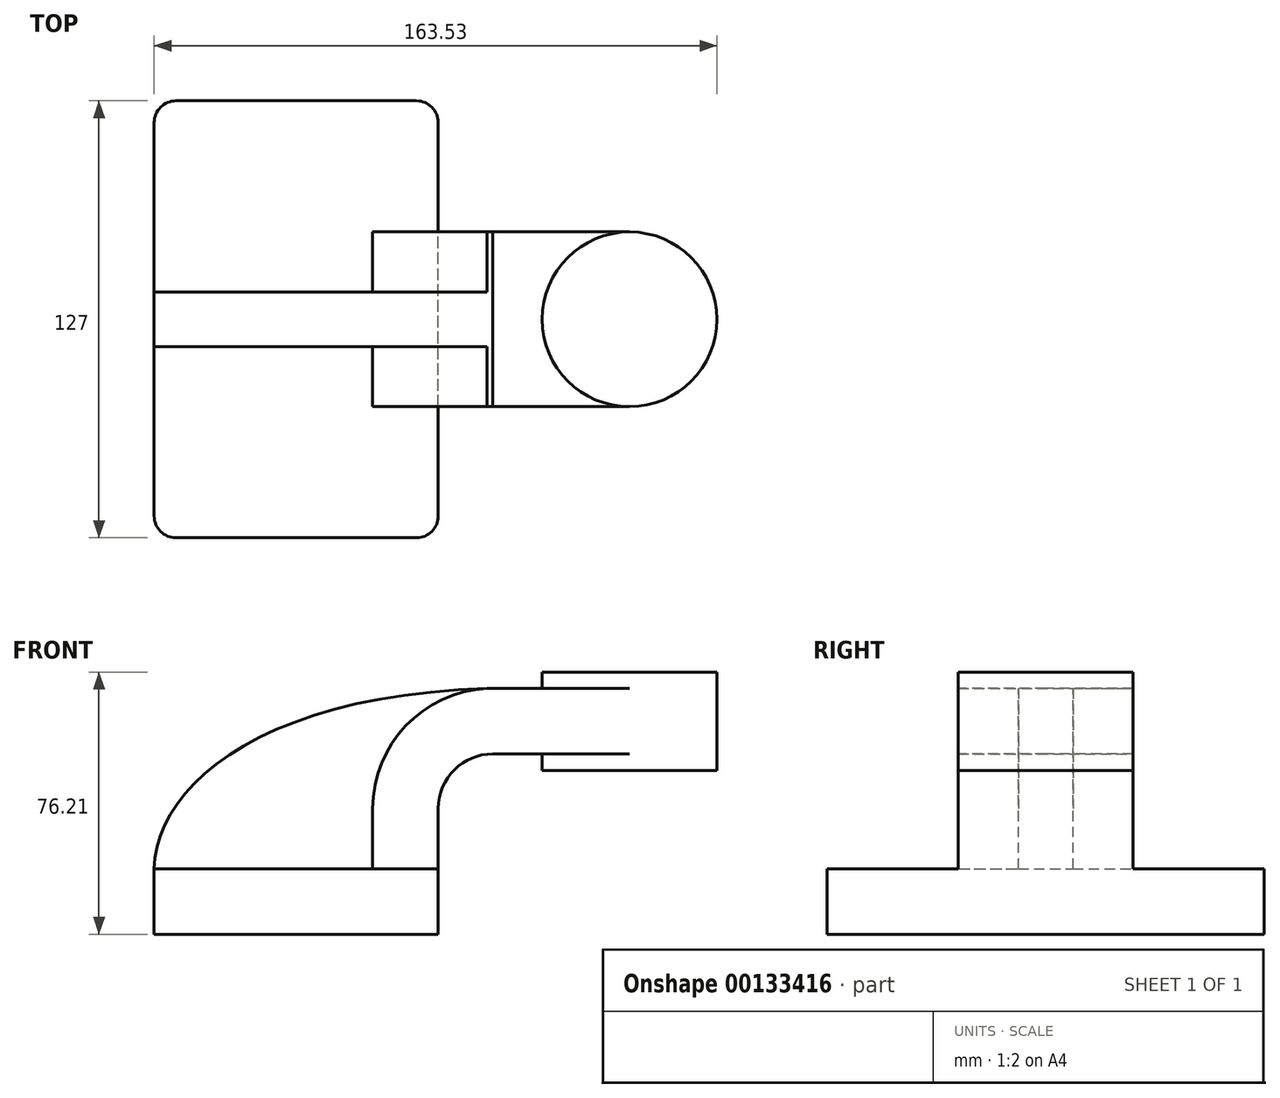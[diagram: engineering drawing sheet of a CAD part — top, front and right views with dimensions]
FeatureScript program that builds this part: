
annotation { "Feature Type Name" : "Feature", "Feature Type Description" : "" }
export const myFeature = defineFeature(function(context is Context, id is Id, definition is map)
    precondition{}
    {
        {
            var Q0;
            Q0=qCreatedBy(makeId("Front.planeOp"),FACE);
            var sketch = newSketch(context, id + "F0", { "sketchPlane" : qUnion([Q0])});
            skLineSegment(sketch, "E0.bottom", {"start": v(41.28, -9.52) * mm, "end": v(-41.27, -9.53) * mm});
            skLineSegment(sketch, "E0.top", {"start": v(41.27, 9.53) * mm, "end": v(-41.28, 9.53) * mm});
            skLineSegment(sketch, "E0.left", {"start": v(41.28, -9.52) * mm, "end": v(41.28, 9.53) * mm});
            skLineSegment(sketch, "E0.right", {"start": v(-41.27, -9.53) * mm, "end": v(-41.28, 9.53) * mm});
            skPoint(sketch, "E0.middle", {"position": v(0, 0) * mm});
            skLineSegment(sketch, "E1.bottom", {"start": v(122.25, 38.1) * mm, "end": v(71.45, 38.1) * mm});
            skLineSegment(sketch, "E1.top", {"start": v(122.25, 66.68) * mm, "end": v(71.45, 66.68) * mm});
            skLineSegment(sketch, "E1.left", {"start": v(122.25, 38.1) * mm, "end": v(122.25, 66.68) * mm});
            skLineSegment(sketch, "E1.right", {"start": v(71.45, 38.1) * mm, "end": v(71.45, 66.68) * mm});
            skPoint(sketch, "E1.middle", {"position": v(96.85, 52.39) * mm});
            skLineSegment(sketch, "E2", {"start": v(41.27, 9.53) * mm, "end": v(41.27, 27) * mm});
            skArc(sketch, "E3", {"start": v(41.27, 27) * mm, "mid": v(45.92, 38.23) * mm, "end": v(57.15, 42.88) * mm});
            skLineSegment(sketch, "E4", {"start": v(57.15, 42.88) * mm, "end": v(96.85, 42.88) * mm});
            skLineSegment(sketch, "E5.0", {"start": v(57.15, 61.93) * mm, "end": v(96.85, 61.93) * mm});
            skArc(sketch, "E5.1", {"start": v(22.23, 27) * mm, "mid": v(32.45, 51.7) * mm, "end": v(57.15, 61.93) * mm});
            skLineSegment(sketch, "E5.2", {"start": v(22.22, 9.53) * mm, "end": v(22.22, 27) * mm});
            skFitSpline(sketch, "E6", {"points": [v(-41.28, 9.52) * mm, v(57.15, 61.93) * mm], "startDerivative": vector(1.84, 72.05) * mm, "endDerivative": vector(201.06, 4.4) * mm});
            skLineSegment(sketch, "E7", {"start": v(96.85, 38.1) * mm, "end": v(96.85, 66.68) * mm});
            skSolve(sketch);
        }
        {
            var Q0;
            Q0=makeQuery(id+"F0.imprint","IMPRINT",FACE,{"disambiguationData":[TD([[makeQuery(id+"F0.imprint","IMPRINT",EDGE,{"derivedFrom":sQuery(id+"F0.wireOp",EDGE,"E0.bottom")}),-1.0]])]});
            extrude(context, id + "F1", {"entities" : qUnion([Q0]), "endBound" : BoundingType.SYMMETRIC, "depth" : 127 * mm});
        }
        {
            var Q0;
            {var subQ1=sQuery(id+"F0.wireOp",EDGE,"E2");Q0=makeQuery(id+"F0.imprint","IMPRINT",FACE,{"disambiguationData":[TD([[makeQuery(id+"F0.imprint","IMPRINT",EDGE,{"derivedFrom":subQ1}),1.0]])]});}
            var Q1;
            {var subQ0=sQuery(id+"F0.wireOp",EDGE,"E4");var subQ1=sQuery(id+"F0.wireOp",EDGE,"E1.right");var subQ2=makeQuery(id+"F0.imprint","INTERSECT",VERTEX,{"derivedFrom":[subQ1,subQ0]});Q1=makeQuery(id+"F0.imprint","IMPRINT",FACE,{"disambiguationData":[TD([[makeQuery(id+"F0.imprint","IMPRINT",EDGE,{"disambiguationData":[TD([[subQ2,-1.0]])],"derivedFrom":subQ1}),-1.0]])]});}
            extrude(context, id + "F2", {"entities" : qUnion([Q0, Q1]), "operationType" : NewBodyOperationType.ADD, "endBound" : BoundingType.SYMMETRIC, "depth" : 50.8 * mm});
        }
        {
            var Q0;
            {var subQ3=sQuery(id+"F0.wireOp",EDGE,"E5.2");Q0=makeQuery(id+"F0.imprint","IMPRINT",FACE,{"disambiguationData":[TD([[makeQuery(id+"F0.imprint","IMPRINT",EDGE,{"derivedFrom":subQ3}),1.0]])]});}
            extrude(context, id + "F3", {"entities" : qUnion([Q0]), "operationType" : NewBodyOperationType.ADD, "endBound" : BoundingType.SYMMETRIC, "depth" : 15.88 * mm});
        }
        {
            var Q0;
            {var subQ4=sQuery(id+"F0.wireOp",EDGE,"E1.left");Q0=makeQuery(id+"F0.imprint","IMPRINT",FACE,{"disambiguationData":[TD([[makeQuery(id+"F0.imprint","IMPRINT",EDGE,{"derivedFrom":subQ4}),1.0]])]});}
            var Q1;
            Q1=sQuery(id+"F0.wireOp",EDGE,"E7");
            revolve(context, id + "F4", {"operationType" : NewBodyOperationType.ADD, "entities" : qUnion([Q0]), "axis" : qUnion([Q1]), "revolveType" : RevolveType.FULL});
        }
        {
            var Q0;
            Q0=makeQuery(id+"F1.opExtrude","CAP_EDGE",EDGE,{"disambiguationData":[OSD([sQuery(id+"F0.wireOp",EDGE,"E0.right")])],"isStart":false});
            var Q1;
            Q1=makeQuery(id+"F1.opExtrude","CAP_EDGE",EDGE,{"disambiguationData":[OSD([sQuery(id+"F0.wireOp",EDGE,"E0.left")])],"isStart":false});
            var Q2;
            Q2=makeQuery(id+"F1.opExtrude","CAP_EDGE",EDGE,{"disambiguationData":[OSD([sQuery(id+"F0.wireOp",EDGE,"E0.right")])],"isStart":true});
            var Q3;
            Q3=makeQuery(id+"F1.opExtrude","CAP_EDGE",EDGE,{"disambiguationData":[OSD([sQuery(id+"F0.wireOp",EDGE,"E0.left")])],"isStart":true});
            fillet(context, id + "F5", {"entities" : qUnion([Q0, Q1, Q2, Q3]), "radius" : 6.35 * mm, "tangentPropagation" : true, "allowEdgeOverflow" : false});
        }
    });
